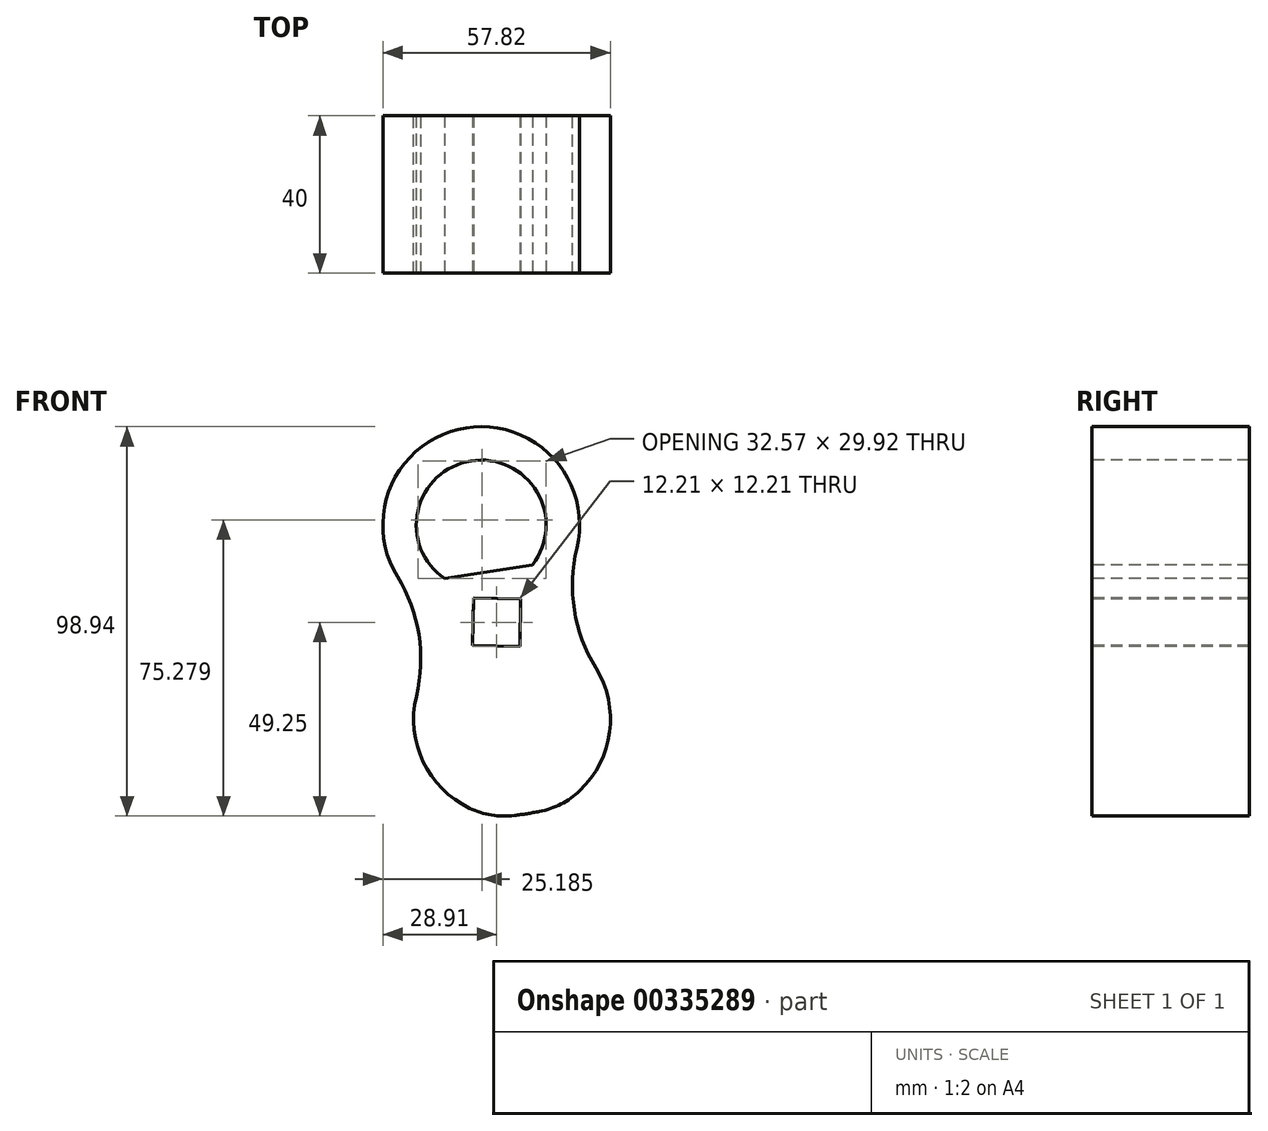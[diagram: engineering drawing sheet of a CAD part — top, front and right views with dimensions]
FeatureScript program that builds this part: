
annotation { "Feature Type Name" : "Feature", "Feature Type Description" : "" }
export const myFeature = defineFeature(function(context is Context, id is Id, definition is map)
    precondition{}
    {
        {
            var Q0;
            Q0=qCreatedBy(makeId("Front.planeOp"),FACE);
            var sketch = newSketch(context, id + "F0", { "sketchPlane" : qUnion([Q0])});
            skCircle(sketch, "E0", {"center": v(-25, 0) * mm, "radius": 25 * mm});
            skCircle(sketch, "E1", {"center": v(25, 0) * mm, "radius": 25 * mm});
            skSolve(sketch);
        }
        {
            var Q0;
            Q0=makeQuery(id+"F0.imprint","IMPRINT",FACE,{"disambiguationData":[TD([[makeQuery(id+"F0.imprint","IMPRINT",EDGE,{"derivedFrom":sQuery(id+"F0.wireOp",EDGE,"E0")}),1.0]])]});
            var Q1;
            Q1=makeQuery(id+"F0.imprint","IMPRINT",FACE,{"disambiguationData":[TD([[makeQuery(id+"F0.imprint","IMPRINT",EDGE,{"derivedFrom":sQuery(id+"F0.wireOp",EDGE,"E1")}),1.0]])]});
            extrude(context, id + "F1", {"entities" : qUnion([Q0, Q1]), "depth" : 40 * mm, "symmetric" : true});
        }
        {
            var Q0;
            Q0=qCreatedBy(makeId("Front.planeOp"),FACE);
            var sketch = newSketch(context, id + "F2", { "sketchPlane" : qUnion([Q0])});
            skCircle(sketch, "E2.0", {"center": v(-25, 0) * mm, "radius": 25 * mm});
            skCircle(sketch, "E3.0", {"center": v(25, 0) * mm, "radius": 25 * mm});
            skArc(sketch, "E4", {"start": v(-15.38, 23.08) * mm, "mid": v(0, 20) * mm, "end": v(15.38, 23.08) * mm});
            skSolve(sketch);
        }
        {
            var Q0;
            {var subQ0=sQuery(id+"F2.wireOp",EDGE,"E4");Q0=makeQuery(id+"F2.imprint","IMPRINT",FACE,{"disambiguationData":[TD([[makeQuery(id+"F2.imprint","IMPRINT",EDGE,{"derivedFrom":subQ0}),-1.0]])]});}
            extrude(context, id + "F3", {"entities" : qUnion([Q0]), "depth" : 40 * mm, "symmetric" : true});
        }
        {
            var Q0;
            Q0=makeQuery(id+"F3.opExtrude","SWEPT_BODY",BODY,{"disambiguationData":[OSD([sQuery(id+"F2.wireOp",EDGE,"E2.0"),sQuery(id+"F2.wireOp",EDGE,"E3.0"),sQuery(id+"F2.wireOp",EDGE,"2BZBx5rq-q8Em-88Co-RqiP-DuQqBopabYor")])]});
            var Q1;
            Q1=qCreatedBy(makeId("Top.planeOp"),FACE);
            mirror(context, id + "F4", {"entities" : qUnion([Q0]), "mirrorPlane" : qUnion([Q1])});
        }
        {
            var Q0;
            Q0=makeQuery(id+"F3.opExtrude","SWEPT_BODY",BODY,{"disambiguationData":[OSD([sQuery(id+"F2.wireOp",EDGE,"E2.0"),sQuery(id+"F2.wireOp",EDGE,"E3.0"),sQuery(id+"F2.wireOp",EDGE,"2BZBx5rq-q8Em-88Co-RqiP-DuQqBopabYor")])]});
            var Q1;
            Q1=makeQuery(id+"F1.opExtrude","SWEPT_BODY",BODY,{"disambiguationData":[OSD([sQuery(id+"F0.wireOp",EDGE,"E1")])]});
            var Q2;
            Q2=makeQuery(id+"F1.opExtrude","SWEPT_BODY",BODY,{"disambiguationData":[OSD([sQuery(id+"F0.wireOp",EDGE,"E0")])]});
            var Q3;
            Q3=makeQuery(id+"F4.opPattern","COPY",BODY,{"derivedFrom":makeQuery(id+"F3.opExtrude","SWEPT_BODY",BODY,{"disambiguationData":[OSD([sQuery(id+"F2.wireOp",EDGE,"E2.0"),sQuery(id+"F2.wireOp",EDGE,"E3.0"),sQuery(id+"F2.wireOp",EDGE,"2BZBx5rq-q8Em-88Co-RqiP-DuQqBopabYor")])]}),"instanceName":"1"});
            booleanBodies(context, id + "F5", {"operationType" : BooleanOperationType.UNION, "tools" : qUnion([Q0, Q1, Q2, Q3])});
        }
        {
            var Q0;
            {var subQ0=makeQuery(id+"F3.opExtrude","CAP_FACE",FACE,{"disambiguationData":[OSD([sQuery(id+"F2.wireOp",EDGE,"E2.0"),sQuery(id+"F2.wireOp",EDGE,"E3.0"),sQuery(id+"F2.wireOp",EDGE,"2BZBx5rq-q8Em-88Co-RqiP-DuQqBopabYor")])],"isStart":false});Q0=makeQuery(id+"F5.opBoolean","MERGE",FACE,{"derivedFrom":[makeQuery(id+"F1.opExtrude","CAP_FACE",FACE,{"disambiguationData":[OSD([sQuery(id+"F0.wireOp",EDGE,"E0")])],"isStart":false}),makeQuery(id+"F1.opExtrude","CAP_FACE",FACE,{"disambiguationData":[OSD([sQuery(id+"F0.wireOp",EDGE,"E1")])],"isStart":false}),subQ0,makeQuery(id+"F4.opPattern","COPY",FACE,{"derivedFrom":subQ0,"instanceName":"1"})]});}
            var sketch = newSketch(context, id + "F6", { "sketchPlane" : qUnion([Q0])});
            skLineSegment(sketch, "E5.bottom", {"start": v(6.95, 4.87) * mm, "end": v(-4.87, 6.95) * mm});
            skLineSegment(sketch, "E5.top", {"start": v(4.87, -6.95) * mm, "end": v(-6.95, -4.87) * mm});
            skLineSegment(sketch, "E5.left", {"start": v(6.95, 4.87) * mm, "end": v(4.87, -6.95) * mm});
            skLineSegment(sketch, "E5.right", {"start": v(-4.87, 6.95) * mm, "end": v(-6.95, -4.87) * mm});
            skPoint(sketch, "E5.middle", {"position": v(0, 0) * mm});
            skSolve(sketch);
        }
        {
            var Q0;
            Q0=makeQuery(id+"F6.imprint","IMPRINT",FACE,{"disambiguationData":[TD([[makeQuery(id+"F6.imprint","IMPRINT",EDGE,{"derivedFrom":sQuery(id+"F6.wireOp",EDGE,"E5.bottom")}),1.0]])]});
            extrude(context, id + "F7", {"entities" : qUnion([Q0]), "operationType" : NewBodyOperationType.REMOVE, "endBound" : BoundingType.THROUGH_ALL, "oppositeDirection" : true, "depth" : 25 * mm});
        }
        {
            var Q0;
            {var subQ0=makeQuery(id+"F3.opExtrude","CAP_FACE",FACE,{"disambiguationData":[OSD([sQuery(id+"F2.wireOp",EDGE,"E2.0"),sQuery(id+"F2.wireOp",EDGE,"E3.0"),sQuery(id+"F2.wireOp",EDGE,"2BZBx5rq-q8Em-88Co-RqiP-DuQqBopabYor")])],"isStart":false});Q0=makeQuery(id+"F5.opBoolean","MERGE",FACE,{"derivedFrom":[makeQuery(id+"F1.opExtrude","CAP_FACE",FACE,{"disambiguationData":[OSD([sQuery(id+"F0.wireOp",EDGE,"E0")])],"isStart":false}),makeQuery(id+"F1.opExtrude","CAP_FACE",FACE,{"disambiguationData":[OSD([sQuery(id+"F0.wireOp",EDGE,"E1")])],"isStart":false}),subQ0,makeQuery(id+"F4.opPattern","COPY",FACE,{"derivedFrom":subQ0,"instanceName":"1"})]});}
            var sketch = newSketch(context, id + "F8", { "sketchPlane" : qUnion([Q0])});
            skCircle(sketch, "E6", {"center": v(25, 0) * mm, "radius": 16.5 * mm});
            skLineSegment(sketch, "E7", {"start": v(13, 11.32) * mm, "end": v(13, -11.32) * mm});
            skSolve(sketch);
        }
        {
            var Q0;
            {var subQ0=sQuery(id+"F8.wireOp",EDGE,"E7");Q0=makeQuery(id+"F8.imprint","IMPRINT",FACE,{"disambiguationData":[TD([[makeQuery(id+"F8.imprint","IMPRINT",EDGE,{"derivedFrom":subQ0}),1.0]])]});}
            extrude(context, id + "F9", {"entities" : qUnion([Q0]), "operationType" : NewBodyOperationType.REMOVE, "endBound" : BoundingType.THROUGH_ALL, "oppositeDirection" : true, "depth" : 25 * mm});
        }
        {
            var Q0;
            {var subQ0=makeQuery(id+"F3.opExtrude","CAP_FACE",FACE,{"disambiguationData":[OSD([sQuery(id+"F2.wireOp",EDGE,"E2.0"),sQuery(id+"F2.wireOp",EDGE,"E3.0"),sQuery(id+"F2.wireOp",EDGE,"E4")])],"isStart":false});Q0=makeQuery(id+"F5.opBoolean","MERGE",FACE,{"derivedFrom":[makeQuery(id+"F1.opExtrude","CAP_FACE",FACE,{"disambiguationData":[OSD([sQuery(id+"F0.wireOp",EDGE,"E0")])],"isStart":false}),makeQuery(id+"F1.opExtrude","CAP_FACE",FACE,{"disambiguationData":[OSD([sQuery(id+"F0.wireOp",EDGE,"E1")])],"isStart":false}),subQ0,makeQuery(id+"F4.opPattern","COPY",FACE,{"derivedFrom":subQ0,"instanceName":"1"})]});}
            var sketch = newSketch(context, id + "F10", { "sketchPlane" : qUnion([Q0])});
            skArc(sketch, "E8", {"start": v(-48.46, 12.46) * mm, "mid": v(-49.21, -2.8) * mm, "end": v(-47.6, -18) * mm});
            skLineSegment(sketch, "E9", {"start": v(-48.46, 12.46) * mm, "end": v(-58.54, 13.66) * mm});
            skLineSegment(sketch, "E10", {"start": v(-58.54, 13.66) * mm, "end": v(-58.54, -22.82) * mm});
            skLineSegment(sketch, "E11", {"start": v(-58.54, -22.82) * mm, "end": v(-47.6, -18) * mm});
            skSolve(sketch);
        }
        {
            var Q0;
            Q0=qSketchRegion(id+"F10",true);
            extrude(context, id + "F11", {"entities" : qUnion([Q0]), "operationType" : NewBodyOperationType.REMOVE, "oppositeDirection" : true, "depth" : 40 * mm});
        }
        {
            var Q0;
            Q0=makeQuery(id+"FgXtsFG8VJguosy_3.1.F11.boolean.opBoolean","INTERSECT",EDGE,{"disambiguationData":[OD(0.0)],"derivedFrom":[makeQuery(id+"F1.opExtrude","SWEPT_FACE",FACE,{"disambiguationData":[OSD([sQuery(id+"F0.wireOp",EDGE,"E1")])]}),makeQuery(id+"FgXtsFG8VJguosy_3.1.F11.opExtrude","SWEPT_FACE",FACE,{"disambiguationData":[OSD([sQuery(id+"F10.wireOp",EDGE,"E8")])]})]});
            var Q1;
            Q1=makeQuery(id+"FgXtsFG8VJguosy_3.1.F11.boolean.opBoolean","INTERSECT",EDGE,{"disambiguationData":[OD(1.0)],"derivedFrom":[makeQuery(id+"F1.opExtrude","SWEPT_FACE",FACE,{"disambiguationData":[OSD([sQuery(id+"F0.wireOp",EDGE,"E1")])]}),makeQuery(id+"FgXtsFG8VJguosy_3.1.F11.opExtrude","SWEPT_FACE",FACE,{"disambiguationData":[OSD([sQuery(id+"F10.wireOp",EDGE,"E8")])]})]});
            var Q2;
            Q2=makeQuery(id+"F11.boolean.opBoolean","INTERSECT",EDGE,{"disambiguationData":[OD(0.0)],"derivedFrom":[makeQuery(id+"F1.opExtrude","SWEPT_FACE",FACE,{"disambiguationData":[OSD([sQuery(id+"F0.wireOp",EDGE,"E0")])]}),makeQuery(id+"F11.opExtrude","SWEPT_FACE",FACE,{"disambiguationData":[OSD([sQuery(id+"F10.wireOp",EDGE,"E8")])]})]});
            var Q3;
            Q3=makeQuery(id+"F11.boolean.opBoolean","INTERSECT",EDGE,{"disambiguationData":[OD(1.0)],"derivedFrom":[makeQuery(id+"F1.opExtrude","SWEPT_FACE",FACE,{"disambiguationData":[OSD([sQuery(id+"F0.wireOp",EDGE,"E0")])]}),makeQuery(id+"F11.opExtrude","SWEPT_FACE",FACE,{"disambiguationData":[OSD([sQuery(id+"F10.wireOp",EDGE,"E8")])]})]});
            fillet(context, id + "F12", {"entities" : qUnion([Q0, Q1, Q2, Q3]), "radius" : 20.5 * mm, "tangentPropagation" : true, "allowEdgeOverflow" : false});
        }
        {
            var Q0;
            Q0=qCreatedBy(makeId("Top.planeOp"),FACE);
            var sketch = newSketch(context, id + "F13", { "sketchPlane" : qUnion([Q0])});
            skLineSegment(sketch, "E12", {"start": v(0, 39.64) * mm, "end": v(0, -38.69) * mm, "construction": true});
            skSolve(sketch);
        }
        {
            var Q0;
            Q0=makeQuery(id+"F3.opExtrude","SWEPT_BODY",BODY,{"disambiguationData":[OSD([sQuery(id+"F2.wireOp",EDGE,"E2.0"),sQuery(id+"F2.wireOp",EDGE,"E3.0"),sQuery(id+"F2.wireOp",EDGE,"E4")])]});
            var Q1;
            Q1=sQuery(id+"F13.wireOp",EDGE,"E12");
            transform(context, id + "F14", {"entities" : qUnion([Q0]), "transformType" : TransformType.ROTATION, "transformAxis" : qUnion([Q1]), "angle" : 99 * degree, "makeCopy" : false});
        }
    });
